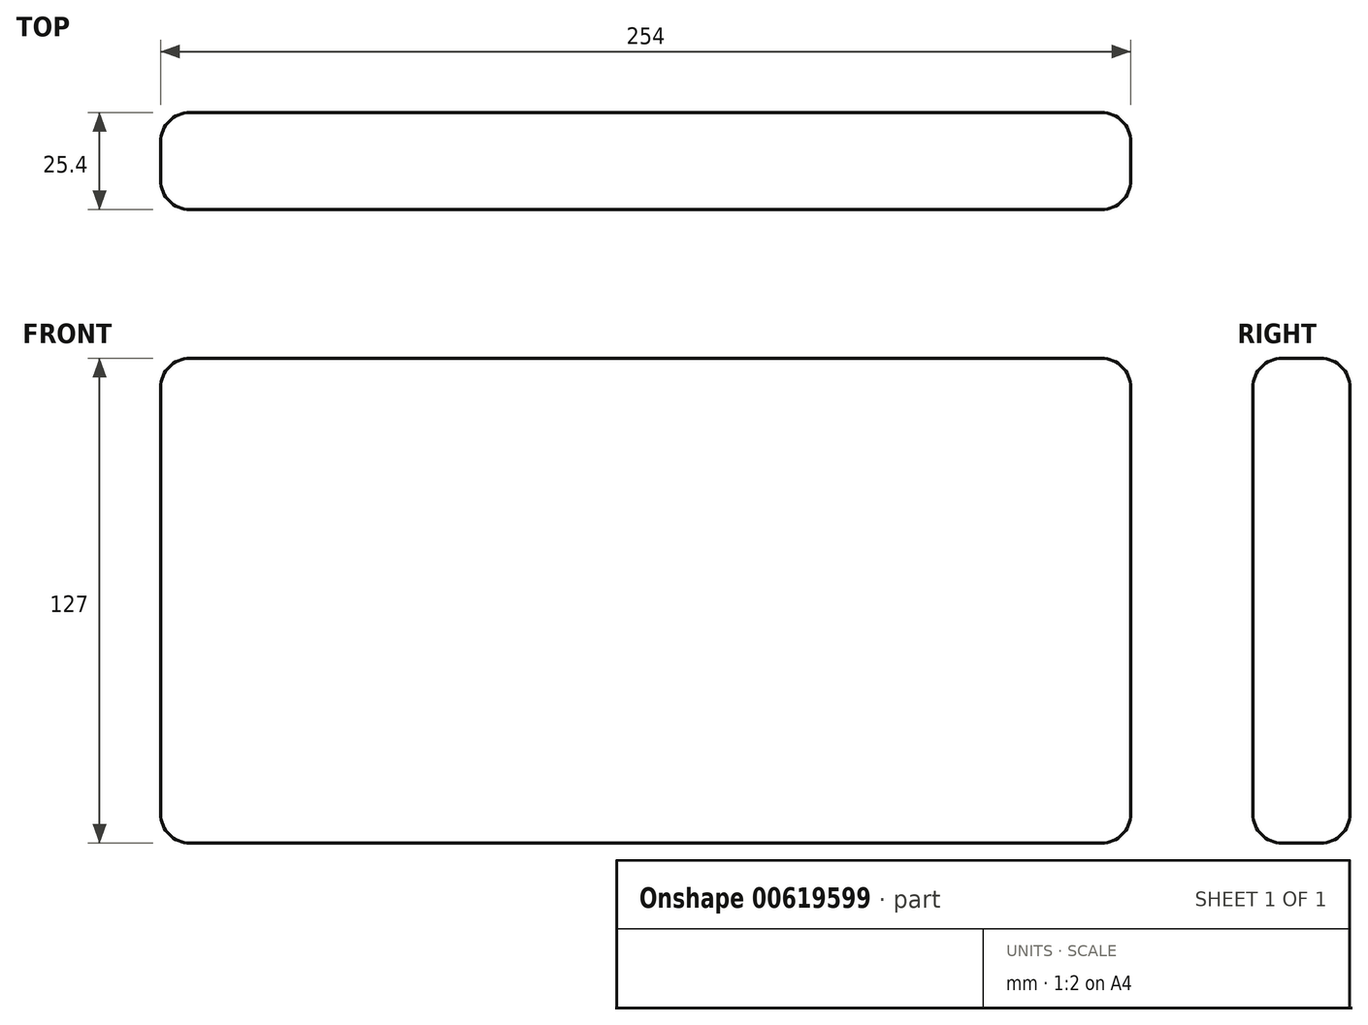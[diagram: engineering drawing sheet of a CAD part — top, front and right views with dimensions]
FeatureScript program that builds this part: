
annotation { "Feature Type Name" : "Feature", "Feature Type Description" : "" }
export const myFeature = defineFeature(function(context is Context, id is Id, definition is map)
    precondition{}
    {
        {
            var Q0;
            Q0=qCreatedBy(makeId("Front.planeOp"),FACE);
            var sketch = newSketch(context, id + "F0", { "sketchPlane" : qUnion([Q0])});
            skLineSegment(sketch, "E0.bottom", {"start": v(127, -63.5) * mm, "end": v(-127, -63.5) * mm});
            skLineSegment(sketch, "E0.top", {"start": v(127, 63.5) * mm, "end": v(-127, 63.5) * mm});
            skLineSegment(sketch, "E0.left", {"start": v(127, -63.5) * mm, "end": v(127, 63.5) * mm});
            skLineSegment(sketch, "E0.right", {"start": v(-127, -63.5) * mm, "end": v(-127, 63.5) * mm});
            skPoint(sketch, "E0.middle", {"position": v(0, 0) * mm});
            skSolve(sketch);
        }
        {
            var Q0;
            Q0 = qSketchRegion(id + "F0", true);
            var Q1;
            Q1=makeQuery(id+"F0.imprint","IMPRINT",FACE,{"disambiguationData":[TD([[makeQuery(id+"F0.imprint","IMPRINT",EDGE,{"derivedFrom":sQuery(id+"F0.wireOp",EDGE,"E0.bottom")}),-1.0]])]});
            extrude(context, id + "F1", {"entities" : qUnion([Q0, Q1]), "depth" : 25.4 * mm, "offsetDistance" : 25.4 * mm});
        }
        {
            var Q0;
            Q0=makeQuery(id+"F1.opExtrude","SWEPT_FACE",FACE,{"disambiguationData":[OSD([sQuery(id+"F0.wireOp",EDGE,"E0.bottom")])]});
            var Q1;
            Q1=makeQuery(id+"F1.opExtrude","SWEPT_FACE",FACE,{"disambiguationData":[OSD([sQuery(id+"F0.wireOp",EDGE,"E0.right")])]});
            var Q2;
            Q2=makeQuery(id+"F1.opExtrude","SWEPT_FACE",FACE,{"disambiguationData":[OSD([sQuery(id+"F0.wireOp",EDGE,"E0.left")])]});
            var Q3;
            Q3=makeQuery(id+"F1.opExtrude","SWEPT_FACE",FACE,{"disambiguationData":[OSD([sQuery(id+"F0.wireOp",EDGE,"E0.top")])]});
            fillet(context, id + "F2", {"entities" : qUnion([Q0, Q1, Q2, Q3]), "radius" : 7.62 * mm, "tangentPropagation" : true, "allowEdgeOverflow" : false});
        }
    });
